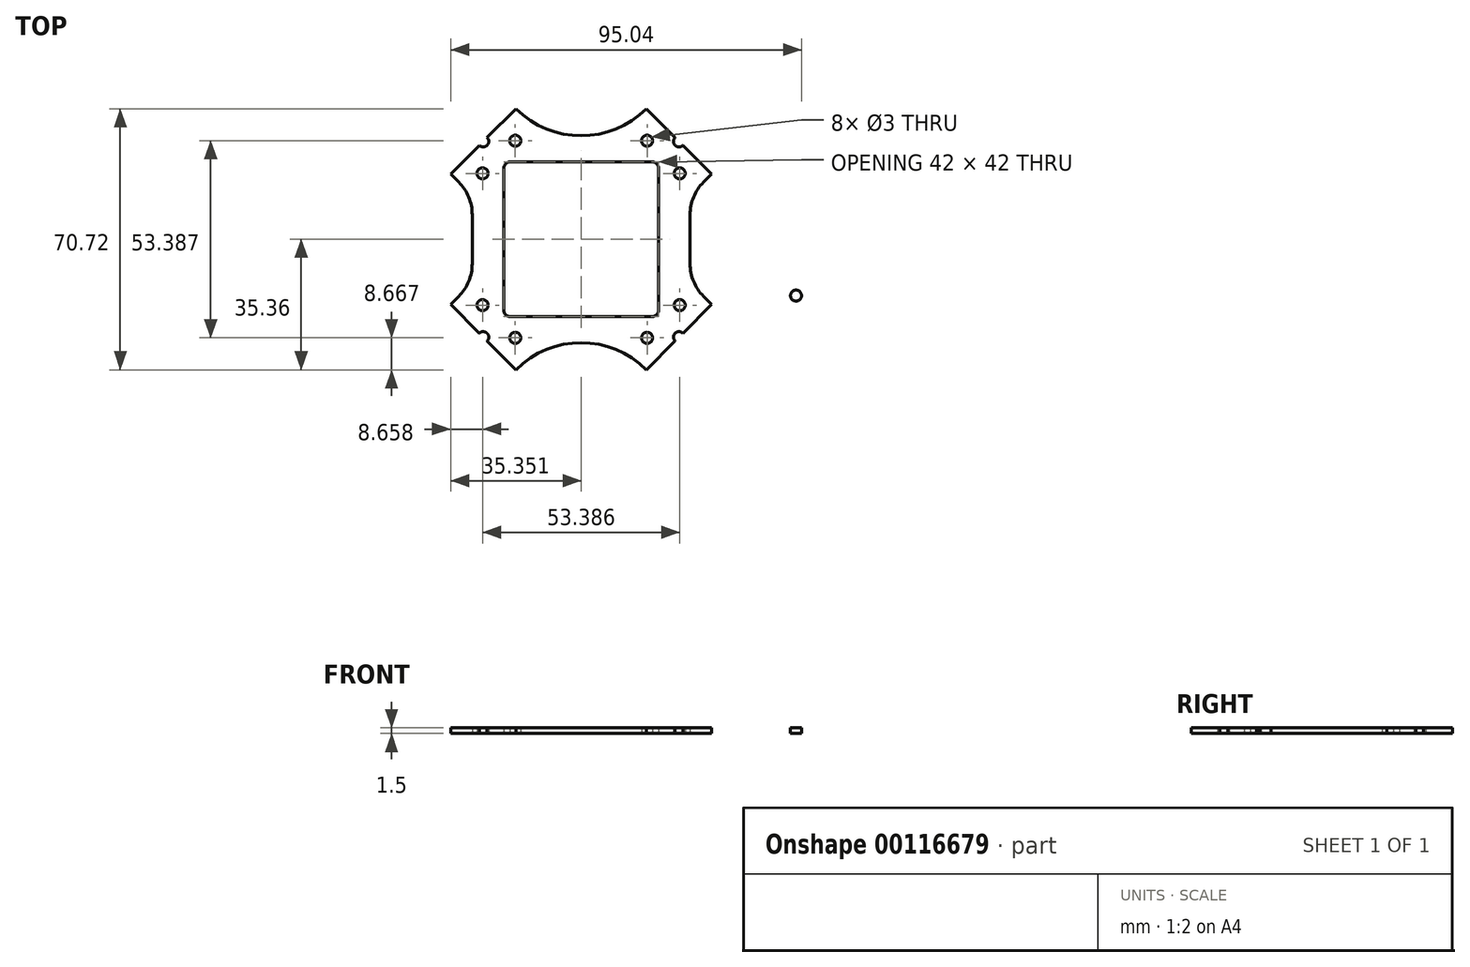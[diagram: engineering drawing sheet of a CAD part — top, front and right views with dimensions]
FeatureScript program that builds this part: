
annotation { "Feature Type Name" : "Feature", "Feature Type Description" : "" }
export const myFeature = defineFeature(function(context is Context, id is Id, definition is map)
    precondition{}
    {
        {
            var Q0;
            Q0=qCreatedBy(makeId("Top.planeOp"),FACE);
            var sketch = newSketch(context, id + "F0", { "sketchPlane" : qUnion([Q0])});
            skLineSegment(sketch, "E0", {"start": v(-66.22, 0) * mm, "end": v(-66.22, -6.64) * mm});
            skArc(sketch, "E1", {"start": v(-69.88, -15.48) * mm, "mid": v(-67.17, -11.43) * mm, "end": v(-66.22, -6.64) * mm});
            skLineSegment(sketch, "E2", {"start": v(-7.22, 0) * mm, "end": v(-7.22, -6.64) * mm});
            skArc(sketch, "E3", {"start": v(-7.22, -6.64) * mm, "mid": v(-6.27, -11.43) * mm, "end": v(-3.56, -15.48) * mm});
            skLineSegment(sketch, "E4", {"start": v(-66.22, 0) * mm, "end": v(-66.22, 6.64) * mm});
            skLineSegment(sketch, "E5", {"start": v(-7.22, 0) * mm, "end": v(-7.22, 6.64) * mm});
            skArc(sketch, "E6", {"start": v(-3.56, 15.48) * mm, "mid": v(-6.27, 11.43) * mm, "end": v(-7.22, 6.64) * mm});
            skArc(sketch, "E7", {"start": v(-54.4, 35.36) * mm, "mid": v(-36.72, 28.03) * mm, "end": v(-19.04, 35.36) * mm});
            skArc(sketch, "E8", {"start": v(-66.22, 6.64) * mm, "mid": v(-67.17, 11.43) * mm, "end": v(-69.88, 15.48) * mm});
            skArc(sketch, "E9", {"start": v(-19.04, -35.36) * mm, "mid": v(-36.72, -28.03) * mm, "end": v(-54.4, -35.36) * mm});
            skLineSegment(sketch, "E10", {"start": v(-54.4, 35.36) * mm, "end": v(-62.17, 27.58) * mm});
            skLineSegment(sketch, "E11", {"start": v(-64.3, 25.46) * mm, "end": v(-72.07, 17.68) * mm});
            skCircle(sketch, "E12", {"center": v(-63.41, -17.85) * mm, "radius": 1.5 * mm});
            skCircle(sketch, "E13", {"center": v(-54.57, -26.7) * mm, "radius": 1.5 * mm});
            skCircle(sketch, "E14", {"center": v(-18.86, -26.7) * mm, "radius": 1.5 * mm});
            skCircle(sketch, "E15", {"center": v(-10.03, -17.85) * mm, "radius": 1.5 * mm});
            skCircle(sketch, "E16", {"center": v(-10.03, 17.85) * mm, "radius": 1.5 * mm});
            skCircle(sketch, "E17", {"center": v(-18.86, 26.7) * mm, "radius": 1.5 * mm});
            skCircle(sketch, "E18", {"center": v(-54.57, 26.7) * mm, "radius": 1.5 * mm});
            skCircle(sketch, "E19", {"center": v(-63.41, 17.85) * mm, "radius": 1.5 * mm});
            skLineSegment(sketch, "E20", {"start": v(-3.56, -15.48) * mm, "end": v(-1.36, -17.68) * mm});
            skLineSegment(sketch, "E21", {"start": v(-3.56, 15.48) * mm, "end": v(-1.36, 17.68) * mm});
            skLineSegment(sketch, "E22", {"start": v(-69.88, 15.48) * mm, "end": v(-72.07, 17.68) * mm});
            skLineSegment(sketch, "E23", {"start": v(-72.07, -17.68) * mm, "end": v(-69.88, -15.48) * mm});
            skLineSegment(sketch, "E24", {"start": v(-55.72, 21) * mm, "end": v(-17.72, 21) * mm});
            skArc(sketch, "E25", {"start": v(-55.72, 21) * mm, "mid": v(-57.13, 20.41) * mm, "end": v(-57.72, 19) * mm});
            skLineSegment(sketch, "E26", {"start": v(-15.72, 19) * mm, "end": v(-15.72, -19) * mm});
            skArc(sketch, "E27", {"start": v(-15.72, 19) * mm, "mid": v(-16.3, 20.41) * mm, "end": v(-17.72, 21) * mm});
            skLineSegment(sketch, "E28", {"start": v(-17.72, -21) * mm, "end": v(-55.72, -21) * mm});
            skArc(sketch, "E29", {"start": v(-17.72, -21) * mm, "mid": v(-16.3, -20.41) * mm, "end": v(-15.72, -19) * mm});
            skLineSegment(sketch, "E30", {"start": v(-57.72, -19) * mm, "end": v(-57.72, 19) * mm});
            skArc(sketch, "E31", {"start": v(-57.72, -19) * mm, "mid": v(-57.13, -20.41) * mm, "end": v(-55.72, -21) * mm});
            skArc(sketch, "E32", {"start": v(-64.3, 25.46) * mm, "mid": v(-62.17, 25.46) * mm, "end": v(-62.17, 27.58) * mm});
            skLineSegment(sketch, "E33", {"start": v(-72.07, -17.68) * mm, "end": v(-64.3, -25.46) * mm});
            skLineSegment(sketch, "E34", {"start": v(-62.17, -27.58) * mm, "end": v(-54.4, -35.36) * mm});
            skArc(sketch, "E35", {"start": v(-62.17, -27.58) * mm, "mid": v(-62.17, -25.46) * mm, "end": v(-64.3, -25.46) * mm});
            skLineSegment(sketch, "E36", {"start": v(-19.04, -35.36) * mm, "end": v(-11.26, -27.58) * mm});
            skLineSegment(sketch, "E37", {"start": v(-9.14, -25.46) * mm, "end": v(-1.36, -17.68) * mm});
            skArc(sketch, "E38", {"start": v(-9.14, -25.46) * mm, "mid": v(-11.26, -25.46) * mm, "end": v(-11.26, -27.58) * mm});
            skLineSegment(sketch, "E39", {"start": v(-1.36, 17.68) * mm, "end": v(-9.14, 25.46) * mm});
            skLineSegment(sketch, "E40", {"start": v(-11.26, 27.58) * mm, "end": v(-19.04, 35.36) * mm});
            skArc(sketch, "E41", {"start": v(-11.26, 27.58) * mm, "mid": v(-11.26, 25.46) * mm, "end": v(-9.14, 25.46) * mm});
            skCircle(sketch, "E42", {"center": v(21.47, -15.25) * mm, "radius": 1.5 * mm});
            skCircle(sketch, "E43", {"center": v(51.97, -15.25) * mm, "radius": 1.5 * mm});
            skArc(sketch, "E44", {"start": v(12.22, -10) * mm, "mid": v(13.72, -11.5) * mm, "end": v(15.22, -10) * mm});
            skLineSegment(sketch, "E45", {"start": v(15.22, 0) * mm, "end": v(15.22, -10) * mm});
            skLineSegment(sketch, "E46", {"start": v(12.22, -10) * mm, "end": v(12.22, 0) * mm});
            skArc(sketch, "E47", {"start": v(58.22, -10) * mm, "mid": v(59.72, -11.5) * mm, "end": v(61.22, -10) * mm});
            skLineSegment(sketch, "E48", {"start": v(61.22, 0) * mm, "end": v(61.22, -10) * mm});
            skLineSegment(sketch, "E49", {"start": v(58.22, -10) * mm, "end": v(58.22, 0) * mm});
            skLineSegment(sketch, "E50", {"start": v(7.22, 0) * mm, "end": v(7.22, -6.64) * mm});
            skArc(sketch, "E51", {"start": v(3.56, -15.48) * mm, "mid": v(6.27, -11.43) * mm, "end": v(7.22, -6.64) * mm});
            skLineSegment(sketch, "E52", {"start": v(66.22, 0) * mm, "end": v(66.22, -6.64) * mm});
            skArc(sketch, "E53", {"start": v(66.22, -6.64) * mm, "mid": v(67.17, -11.43) * mm, "end": v(69.88, -15.48) * mm});
            skCircle(sketch, "E54", {"center": v(21.47, 15.25) * mm, "radius": 1.5 * mm});
            skCircle(sketch, "E55", {"center": v(51.97, 15.25) * mm, "radius": 1.5 * mm});
            skArc(sketch, "E56", {"start": v(15.22, 10) * mm, "mid": v(13.72, 11.5) * mm, "end": v(12.22, 10) * mm});
            skLineSegment(sketch, "E57", {"start": v(15.22, 0) * mm, "end": v(15.22, 10) * mm});
            skLineSegment(sketch, "E58", {"start": v(12.22, 10) * mm, "end": v(12.22, 0) * mm});
            skArc(sketch, "E59", {"start": v(61.22, 10) * mm, "mid": v(59.72, 11.5) * mm, "end": v(58.22, 10) * mm});
            skLineSegment(sketch, "E60", {"start": v(61.22, 0) * mm, "end": v(61.22, 10) * mm});
            skLineSegment(sketch, "E61", {"start": v(58.22, 10) * mm, "end": v(58.22, 0) * mm});
            skLineSegment(sketch, "E62", {"start": v(7.22, 0) * mm, "end": v(7.22, 6.64) * mm});
            skLineSegment(sketch, "E63", {"start": v(66.22, 0) * mm, "end": v(66.22, 6.64) * mm});
            skArc(sketch, "E64", {"start": v(69.88, 15.48) * mm, "mid": v(67.17, 11.43) * mm, "end": v(66.22, 6.64) * mm});
            skArc(sketch, "E65", {"start": v(19.04, 35.36) * mm, "mid": v(36.72, 28.03) * mm, "end": v(54.4, 35.36) * mm});
            skArc(sketch, "E66", {"start": v(7.22, 6.64) * mm, "mid": v(6.27, 11.43) * mm, "end": v(3.56, 15.48) * mm});
            skArc(sketch, "E67", {"start": v(54.4, -35.36) * mm, "mid": v(36.72, -28.03) * mm, "end": v(19.04, -35.36) * mm});
            skLineSegment(sketch, "E68", {"start": v(19.04, 35.36) * mm, "end": v(1.36, 17.68) * mm});
            skLineSegment(sketch, "E69", {"start": v(54.4, 35.36) * mm, "end": v(72.07, 17.68) * mm});
            skLineSegment(sketch, "E70", {"start": v(54.4, -35.36) * mm, "end": v(72.07, -17.68) * mm});
            skLineSegment(sketch, "E71", {"start": v(19.04, -35.36) * mm, "end": v(1.36, -17.68) * mm});
            skCircle(sketch, "E72", {"center": v(10.03, -17.85) * mm, "radius": 1.5 * mm});
            skCircle(sketch, "E73", {"center": v(18.86, -26.7) * mm, "radius": 1.5 * mm});
            skCircle(sketch, "E74", {"center": v(54.57, -26.7) * mm, "radius": 1.5 * mm});
            skCircle(sketch, "E75", {"center": v(63.41, -17.85) * mm, "radius": 1.5 * mm});
            skCircle(sketch, "E76", {"center": v(63.41, 17.85) * mm, "radius": 1.5 * mm});
            skCircle(sketch, "E77", {"center": v(54.57, 26.7) * mm, "radius": 1.5 * mm});
            skCircle(sketch, "E78", {"center": v(18.86, 26.7) * mm, "radius": 1.5 * mm});
            skCircle(sketch, "E79", {"center": v(10.03, 17.85) * mm, "radius": 1.5 * mm});
            skLineSegment(sketch, "E80", {"start": v(1.36, -17.68) * mm, "end": v(3.56, -15.48) * mm});
            skLineSegment(sketch, "E81", {"start": v(1.36, 17.68) * mm, "end": v(3.56, 15.48) * mm});
            skLineSegment(sketch, "E82", {"start": v(69.88, -15.48) * mm, "end": v(72.07, -17.68) * mm});
            skLineSegment(sketch, "E83", {"start": v(69.88, 15.48) * mm, "end": v(72.07, 17.68) * mm});
            skSolve(sketch);
        }
        {
            var Q0;
            Q0=makeQuery(id+"F0.imprint","IMPRINT",FACE,{"disambiguationData":[TD([[makeQuery(id+"F0.imprint","IMPRINT",EDGE,{"derivedFrom":sQuery(id+"F0.wireOp",EDGE,"E0")}),1.0]])]});
            var Q1;
            Q1=makeQuery(id+"F0.imprint","IMPRINT",FACE,{"disambiguationData":[TD([[makeQuery(id+"F0.imprint","IMPRINT",EDGE,{"derivedFrom":sQuery(id+"F0.wireOp",EDGE,"E42")}),1.0]])]});
            extrude(context, id + "F1", {"entities" : qUnion([Q0, Q1]), "depth" : 1.5 * mm});
        }
    });
